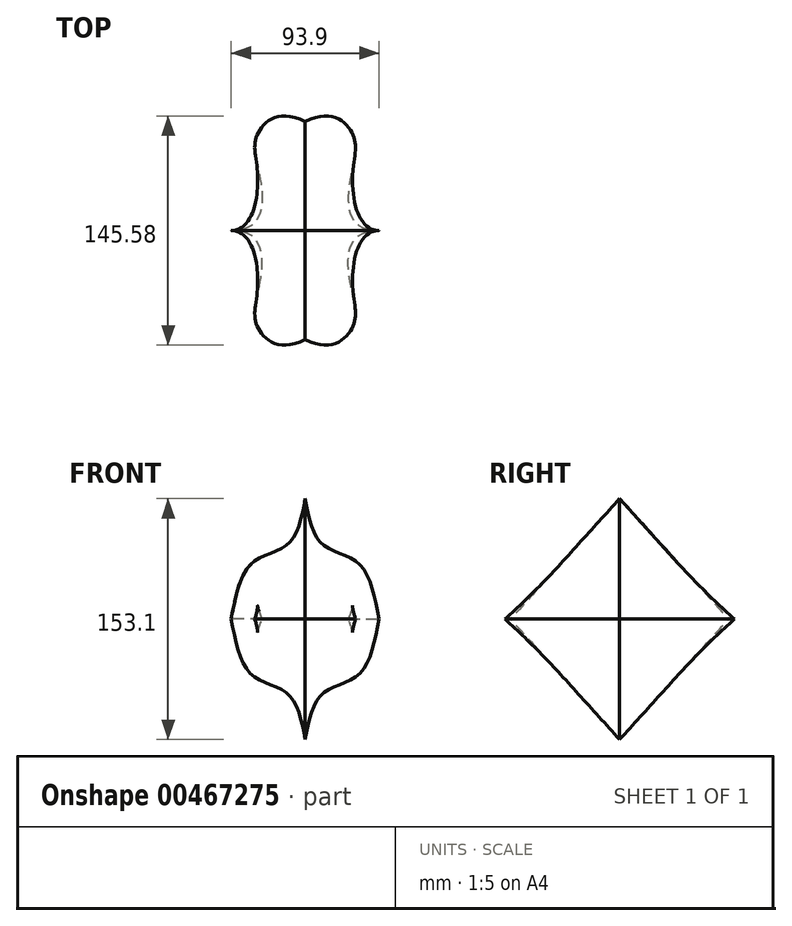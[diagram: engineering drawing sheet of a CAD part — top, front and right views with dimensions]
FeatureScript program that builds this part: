
annotation { "Feature Type Name" : "Feature", "Feature Type Description" : "" }
export const myFeature = defineFeature(function(context is Context, id is Id, definition is map)
    precondition{}
    {
        {
            var Q0;
            Q0=qCreatedBy(makeId("Top.planeOp"),FACE);
            var sketch = newSketch(context, id + "F0", { "sketchPlane" : qUnion([Q0])});
            skFitSpline(sketch, "E0", {"points": [v(0, 69.25) * mm, v(-30.7, 60) * mm, v(-29.09, 35.52) * mm, v(-46.1, 0) * mm], "startDerivative": vector(-157.83, 80.06) * mm, "endDerivative": vector(-181.32, 0) * mm});
            skSolve(sketch);
        }
        {
            var Q0;
            Q0=qCreatedBy(makeId("Front.planeOp"),FACE);
            var sketch = newSketch(context, id + "F1", { "sketchPlane" : qUnion([Q0])});
            skFitSpline(sketch, "E1", {"points": [v(-46.95, 0) * mm, v(-33.76, 35.54) * mm, v(-11.06, 47.46) * mm, v(0, 76.55) * mm], "startDerivative": vector(21.71, 116.9) * mm, "endDerivative": vector(19.23, 104.46) * mm});
            skSolve(sketch);
        }
        {
            var Q0;
            Q0=sQuery(id+"F1.wireOp",EDGE,"E1");
            var Q1;
            Q1=sQuery(id+"F0.wireOp",EDGE,"E0");
            loft(context, id + "F2", {"bodyType" : ToolBodyType.SURFACE, "wireProfilesArray" : [{ "wireProfileEntities" : qUnion([Q0]) }, { "wireProfileEntities" : qUnion([Q1]) }]});
        }
        {
            var Q0;
            Q0=makeQuery(id+"F2.opLoft","SWEPT_BODY",BODY,{"disambiguationData":[OSD([sQuery(id+"F0.wireOp",EDGE,"E0"),sQuery(id+"F1.wireOp",EDGE,"E1")])]});
            var Q1;
            Q1=qCreatedBy(makeId("Right.planeOp"),FACE);
            mirror(context, id + "F3", {"entities" : qUnion([Q0]), "mirrorPlane" : qUnion([Q1])});
        }
        {
            var Q0;
            Q0=makeQuery(id+"F2.opLoft","SWEPT_BODY",BODY,{"disambiguationData":[OSD([sQuery(id+"F0.wireOp",EDGE,"E0"),sQuery(id+"F1.wireOp",EDGE,"E1")])]});
            var Q1;
            Q1=makeQuery(id+"F3.opPattern","COPY",BODY,{"derivedFrom":makeQuery(id+"F2.opLoft","SWEPT_BODY",BODY,{"disambiguationData":[OSD([sQuery(id+"F0.wireOp",EDGE,"E0"),sQuery(id+"F1.wireOp",EDGE,"E1")])]}),"instanceName":"1"});
            var Q2;
            Q2=qCreatedBy(makeId("Front.planeOp"),FACE);
            mirror(context, id + "F4", {"entities" : qUnion([Q0, Q1]), "mirrorPlane" : qUnion([Q2])});
        }
        {
            var Q0;
            Q0=makeQuery(id+"F2.opLoft","SWEPT_BODY",BODY,{"disambiguationData":[OSD([sQuery(id+"F0.wireOp",EDGE,"E0"),sQuery(id+"F1.wireOp",EDGE,"E1")])]});
            var Q1;
            Q1=makeQuery(id+"F4.opPattern","COPY",BODY,{"derivedFrom":makeQuery(id+"F2.opLoft","SWEPT_BODY",BODY,{"disambiguationData":[OSD([sQuery(id+"F0.wireOp",EDGE,"E0"),sQuery(id+"F1.wireOp",EDGE,"E1")])]}),"instanceName":"1"});
            var Q2;
            Q2=makeQuery(id+"F4.opPattern","COPY",BODY,{"derivedFrom":makeQuery(id+"F3.opPattern","COPY",BODY,{"derivedFrom":makeQuery(id+"F2.opLoft","SWEPT_BODY",BODY,{"disambiguationData":[OSD([sQuery(id+"F0.wireOp",EDGE,"E0"),sQuery(id+"F1.wireOp",EDGE,"E1")])]}),"instanceName":"1"}),"instanceName":"1"});
            var Q3;
            Q3=makeQuery(id+"F3.opPattern","COPY",BODY,{"derivedFrom":makeQuery(id+"F2.opLoft","SWEPT_BODY",BODY,{"disambiguationData":[OSD([sQuery(id+"F0.wireOp",EDGE,"E0"),sQuery(id+"F1.wireOp",EDGE,"E1")])]}),"instanceName":"1"});
            var Q4;
            Q4=qCreatedBy(makeId("Top.planeOp"),FACE);
            mirror(context, id + "F5", {"entities" : qUnion([Q0, Q1, Q2, Q3]), "mirrorPlane" : qUnion([Q4])});
        }
    });
